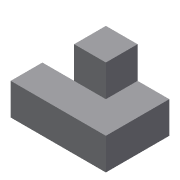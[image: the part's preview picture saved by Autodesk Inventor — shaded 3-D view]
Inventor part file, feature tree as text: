
AUTODESK INVENTOR PART (.ipt)
format: ipt  version: 2015 (Build 190159000, 159)  size: 81,920 bytes
history: native  units: in
note: dims shown in document units (in); Inventor stores cm internally (conversion verified against a paired STEP export)
features: extrude x2, sketch x2
ambient origin geometry x8: Origin, YZ Plane, XZ Plane, XY Plane, X Axis, Y Axis, Z Axis, Center Point
bodies: Solid1 (feature_tree)
feature tree (4):
  extrude  "Extrusion1"  Depth=1.0in
  extrude  "Extrusion2"  Depth=1.0in
  sketch  "Sketch1"  dims[d0=3.0in d1=1.0in]
  sketch  "Sketch2"  dims[d2=1.0in d3=1.0in d4=2.0in d5=1.0in d6=0.0in d7=1.0in d8=1.0in d9=0.0in]
